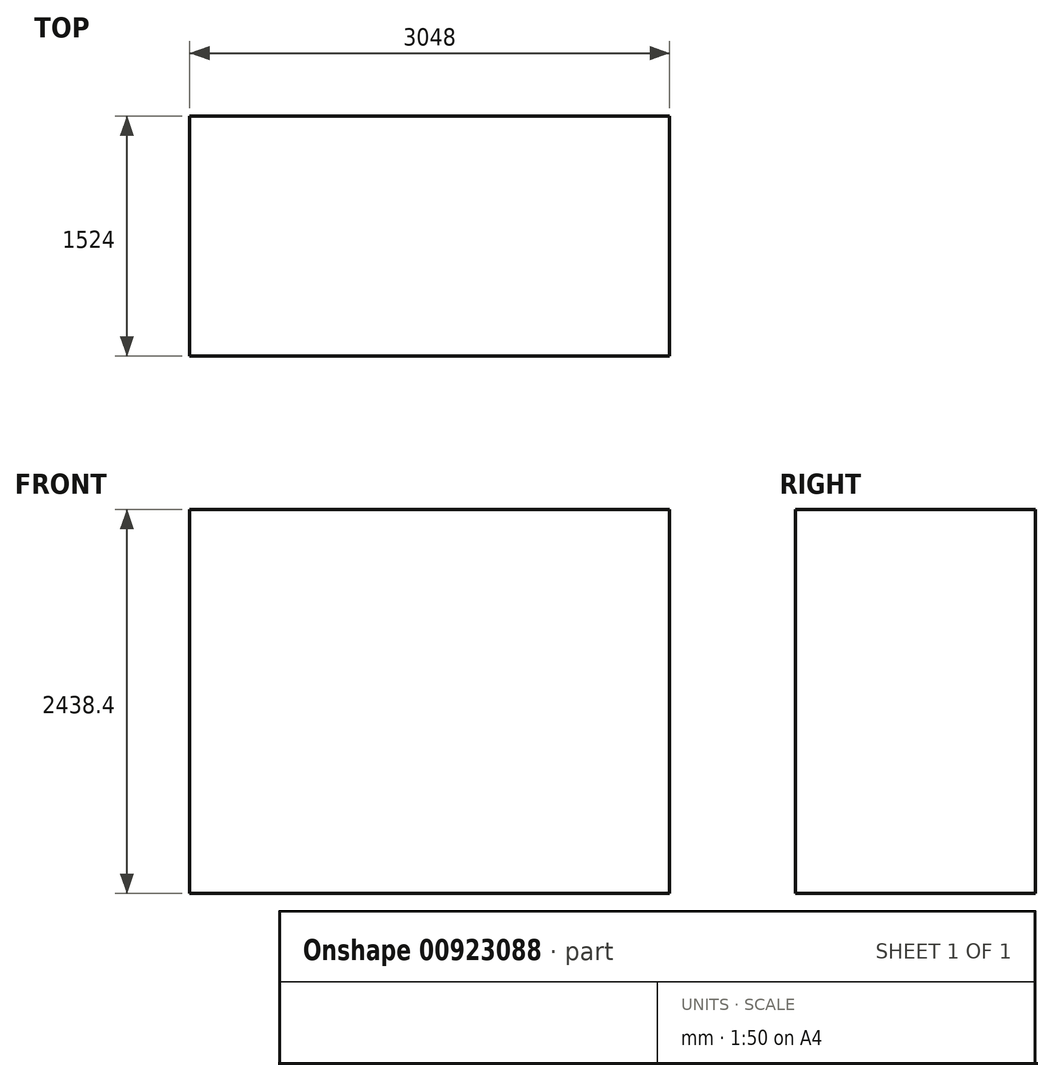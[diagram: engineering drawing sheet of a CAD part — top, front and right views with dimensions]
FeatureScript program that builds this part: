
annotation { "Feature Type Name" : "Feature", "Feature Type Description" : "" }
export const myFeature = defineFeature(function(context is Context, id is Id, definition is map)
    precondition{}
    {
        {
            var Q0;
            Q0=qCreatedBy(makeId("Top.planeOp"),FACE);
            var sketch = newSketch(context, id + "F0", { "sketchPlane" : qUnion([Q0])});
            skLineSegment(sketch, "E0.bottom", {"start": v(1524, 762) * mm, "end": v(-1524, 762) * mm});
            skLineSegment(sketch, "E0.top", {"start": v(1524, -762) * mm, "end": v(-1524, -762) * mm});
            skLineSegment(sketch, "E0.left", {"start": v(1524, 762) * mm, "end": v(1524, -762) * mm});
            skLineSegment(sketch, "E0.right", {"start": v(-1524, 762) * mm, "end": v(-1524, -762) * mm});
            skPoint(sketch, "E0.middle", {"position": v(0, 0) * mm});
            skSolve(sketch);
        }
        {
            var Q0;
            Q0=makeQuery(id+"F0.imprint","IMPRINT",FACE,{"disambiguationData":[TD([[makeQuery(id+"F0.imprint","IMPRINT",EDGE,{"derivedFrom":sQuery(id+"F0.wireOp",EDGE,"E0.bottom")}),1.0]])]});
            extrude(context, id + "F1", {"entities" : qUnion([Q0]), "depth" : 2438.4 * mm, "offsetDistance" : 25.4 * mm});
        }
    });
